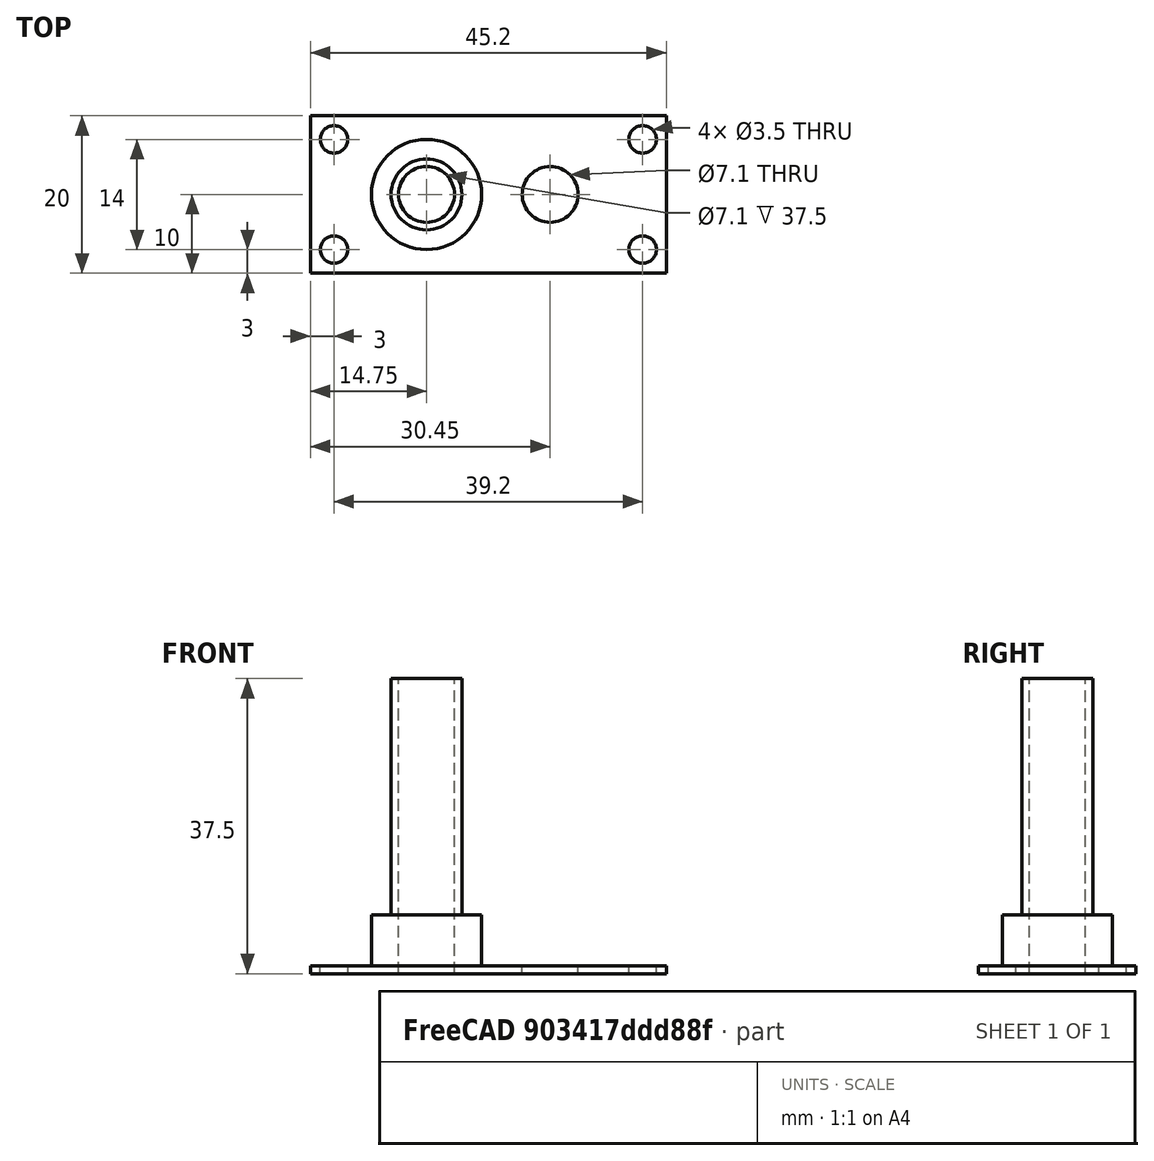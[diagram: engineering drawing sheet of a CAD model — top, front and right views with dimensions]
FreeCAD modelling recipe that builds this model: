
FCSTD DOCUMENT  (FreeCAD 0.17R13522 (Git))
Label: base1_media_con_soportes_v4
License: CreativeCommons Attribution-ShareAlike
LicenseURL: http://creativecommons.org/licenses/by-sa/4.0/
objects: Part::Cut×9, Part::Feature×6, Part::Box×4, Part::Cylinder×4, Part::Fuse×4, Part::Chamfer×3
note: 30 computed .brp shape members not serialized (recipe doc carries the construction recipe); baked Part::Feature solids carry a one-line shape summary decoded from their .brp

FEATURE [Part::Box] Box  label="base"
  AttacherType = Attacher::AttachEngine3D
  Height = 2
  Length = 45.2
  Width = 20
FEATURE [Part::Cylinder] Cylinder  label="cortador izquierda"
  Angle = 360
  AttacherType = Attacher::AttachEngine3D
  Height = 60
  Placement = pos=(14.75,10,-12) rot=(0,0,1;0rad)
  Radius = 3.55
FEATURE [Part::Feature] Cylinder001  label="cortador derecha"
  Placement = pos=(30.45,10,-4) rot=(0,0,1;0rad)
  shape: bbox 7.1 x 7.1 x 10 mm, 3 faces (baked)
FEATURE [Part::Cylinder] Cylinder002  label="sacabocado_abajo_izq"
  Angle = 360
  AttacherType = Attacher::AttachEngine3D
  Height = 10
  Placement = pos=(3,3,-4) rot=(0,0,1;0rad)
  Radius = 1.75
FEATURE [Part::Feature] Cylinder002001  label="sacabocado_abajo_derecha"
  Placement = pos=(42.2,3,-4) rot=(0,0,1;0rad)
  shape: bbox 3.5 x 3.5 x 10 mm, 3 faces (baked)
FEATURE [Part::Feature] Cylinder002002  label="sacabocado_arriba_izq"
  Placement = pos=(3,17,-4) rot=(0,0,1;0rad)
  shape: bbox 3.5 x 3.5 x 10 mm, 3 faces (baked)
FEATURE [Part::Feature] Cylinder002002001  label="sacabocado_arriba_derecha"
  Placement = pos=(42.2,17,-4) rot=(0,0,1;0rad)
  shape: bbox 3.5 x 3.5 x 10 mm, 3 faces (baked)
FEATURE [Part::Cylinder] Cylinder002002002  label="cilindro interior"
  Angle = 360
  AttacherType = Attacher::AttachEngine3D
  Height = 38.5
  Placement = pos=(14.75,10,0) rot=(0,0,1;0rad)
  Radius = 4.5
FEATURE [Part::Cylinder] Cylinder002002003  label="base cilindrica grande"
  Angle = 360
  AttacherType = Attacher::AttachEngine3D
  Height = 8.5
  Placement = pos=(14.75,10,0) rot=(0,0,1;0rad)
  Radius = 7
FEATURE [Part::Cut] Cut
  Base = -> Box
  Refine = true
  Tool = -> Cylinder002
FEATURE [Part::Cut] Cut001
  Base = -> Cut
  Refine = true
  Tool = -> Cylinder002001
FEATURE [Part::Cut] Cut002
  Base = -> Cut001
  Refine = true
  Tool = -> Cylinder001
FEATURE [Part::Cut] Cut003
  Base = -> Cut002
  Refine = true
  Tool = -> Cylinder002002001
FEATURE [Part::Cut] Cut004
  Base = -> Cut003
  Refine = true
  Tool = -> Cylinder002002
FEATURE [Part::Fuse] Fusion
  Base = -> Cylinder002002003
  Refine = true
  Tool = -> Cut004
FEATURE [Part::Fuse] Fusion001
  Base = -> Cylinder002002002
  Refine = true
  Tool = -> Fusion
FEATURE [Part::Cut] Cut005  label="pieza sin soportes"
  Base = -> Fusion001
  Refine = true
  Tool = -> Cylinder
FEATURE [Part::Box] Box001  label="soporte1"
  AttacherType = Attacher::AttachEngine3D
  Height = 10.5
  Length = 5
  Placement = pos=(36.95,7.5,-10.5) rot=(0,0,1;0rad)
  Width = 5
FEATURE [Part::Feature] Box001001  label="soporte2"
  Placement = pos=(18.95,7.5,-10.5) rot=(0,0,1;0rad)
  shape: bbox 5 x 5 x 10.5 mm, 6 faces (baked)
FEATURE [Part::Box] Box001002  label="perforador chavetas"
  AttacherType = Attacher::AttachEngine3D
  Height = 2
  Length = 30
  Placement = pos=(16,8.5,-6.3) rot=(0,0,1;0rad)
  Width = 3
FEATURE [Part::Feature] Box001002001  label="perforador chavetas001"
  Placement = pos=(16,8.5,-6.3) rot=(0,0,1;0rad)
  shape: bbox 30 x 3 x 2 mm, 6 faces (baked)
FEATURE [Part::Cut] Cut006
  Base = -> Box001
  Refine = true
  Tool = -> Box001002
FEATURE [Part::Cut] Cut007
  Base = -> Box001001
  Refine = true
  Tool = -> Box001002001
FEATURE [Part::Fuse] Fusion002
  Base = -> Cut005
  Refine = true
  Tool = -> Cut007
FEATURE [Part::Fuse] Fusion003
  Base = -> Cut006
  Refine = true
  Tool = -> Fusion002
FEATURE [Part::Chamfer] Chamfer
  Base = -> Fusion003
  Edges = 1 edges r=2: [Edge29]
FEATURE [Part::Chamfer] Chamfer001
  Base = -> Chamfer
  Edges = 1 edges r=2: [Edge19]
FEATURE [Part::Chamfer] Chamfer002  label="pieza completa"
  Base = -> Chamfer001
  Edges = 2 edges r=2: [Edge4,Edge10]
FEATURE [Part::Box] Box001002002  label="cortador separa pieza 2"
  AttacherType = Attacher::AttachEngine3D
  Height = 26
  Length = 59
  Placement = pos=(-7.65,-6,-25) rot=(0,0,1;0rad)
  Width = 30
FEATURE [Part::Cut] Cut008
  Base = -> Chamfer002
  Refine = true
  Tool = -> Box001002002
